# Revit family: Soap_Dispenser-Deck_Mounted-Bobrick-SureFlo-B-8281
name_source: partatom
category: Specialty Equipment
units: mm (PartAtom-declared; Revit-internal decimal feet)

## family parameters
Always vertical = No
Cut with Voids When Loaded = No
OmniClass Number = 23.40.20.21.34
OmniClass Title = Soap Holders, Dispensers
Part Type = Normal
Room Calculation Point = No
Round Connector Dimension = Use Diameter
Shared = Yes
Work Plane-Based = Yes

## types (1)
- B-8281
    ADA Compliant = Yes
    Assembly Code = C1030210
    Default Elevation = 0"
    Description = 1" COUNTER-MOUNTED SureFlo®AUTOMATIC TOP-FILL BULK
FOAM SOAP DISPENSER
    Finish - Body = ABS Plastic-Bobrick-Black
    Finish - Soap Bottle = ABS Plastic-Bobrick-White
    Finish - Spout = ABS Plastic-Bobrick-Chrome Plated
    Height = 19 15/16"
    Installation Type = Deck Mounted
    Length = 6 3/4"
    Manufacturer = Bobrick
    Material = ABS Plastic-Bobrick-Chrome Plated
    Model = B-8281
    Price = Prices may vary. Please consult Manufacturer Representative for most up-to-date price list.
    Soap Bottle Capacity = 34-fl oz (1.0-L)
    URL = https://www.bobrick.com
    Width = 3 7/8"

## geometry (parser evidence)
native form markers: Sweep x2
no freeform markers — native parametric forms only
